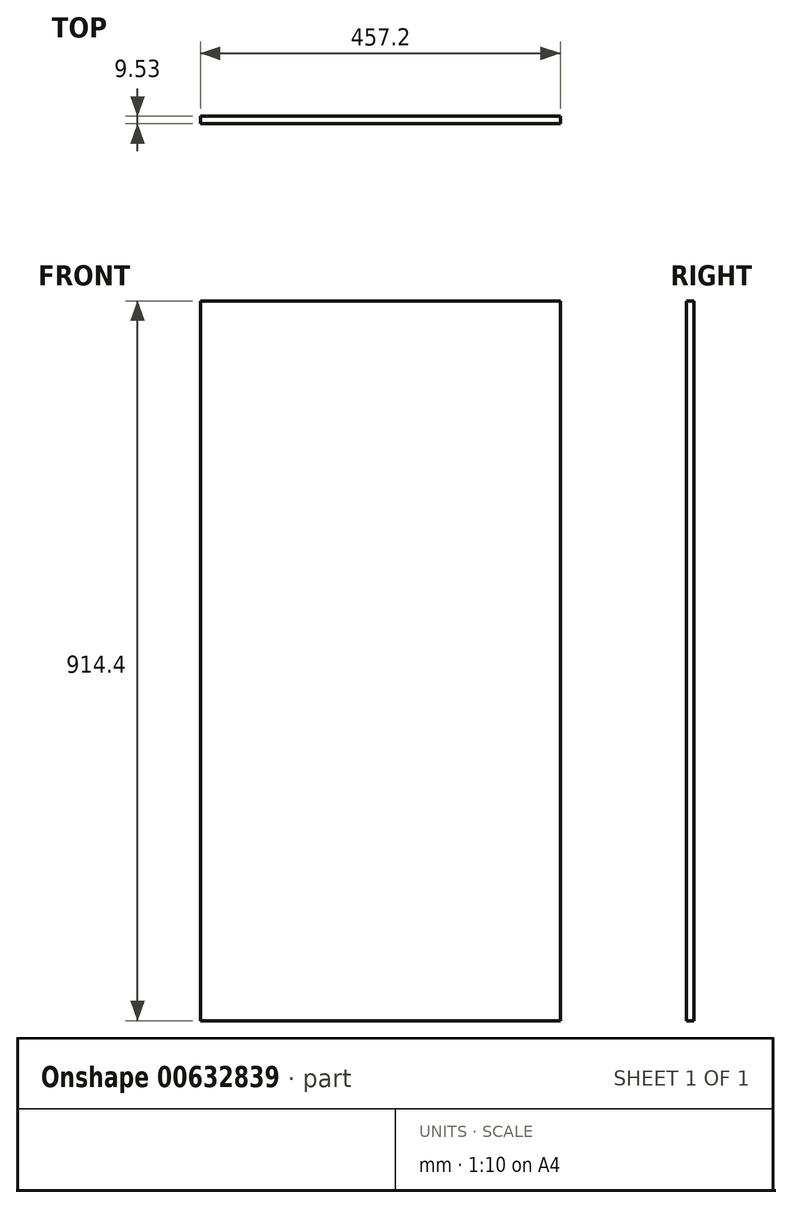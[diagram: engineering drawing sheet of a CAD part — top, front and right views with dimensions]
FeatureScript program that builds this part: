
annotation { "Feature Type Name" : "Feature", "Feature Type Description" : "" }
export const myFeature = defineFeature(function(context is Context, id is Id, definition is map)
    precondition{}
    {
        {
            var Q0;
            Q0=qCreatedBy(makeId("Front.planeOp"),FACE);
            var sketch = newSketch(context, id + "F0", { "sketchPlane" : qUnion([Q0])});
            skLineSegment(sketch, "E0.bottom", {"start": v(228.6, 457.2) * mm, "end": v(-228.6, 457.2) * mm});
            skLineSegment(sketch, "E0.top", {"start": v(228.6, -457.2) * mm, "end": v(-228.6, -457.2) * mm});
            skLineSegment(sketch, "E0.left", {"start": v(228.6, 457.2) * mm, "end": v(228.6, -457.2) * mm});
            skLineSegment(sketch, "E0.right", {"start": v(-228.6, 457.2) * mm, "end": v(-228.6, -457.2) * mm});
            skPoint(sketch, "E0.middle", {"position": v(0, 0) * mm});
            skSolve(sketch);
        }
        {
            var Q0;
            Q0=makeQuery(id+"F0.imprint","IMPRINT",FACE,{"disambiguationData":[TD([[makeQuery(id+"F0.imprint","IMPRINT",EDGE,{"derivedFrom":sQuery(id+"F0.wireOp",EDGE,"E0.bottom")}),1.0]])]});
            extrude(context, id + "F1", {"entities" : qUnion([Q0]), "depth" : 9.52 * mm, "offsetDistance" : 25.4 * mm});
        }
    });
